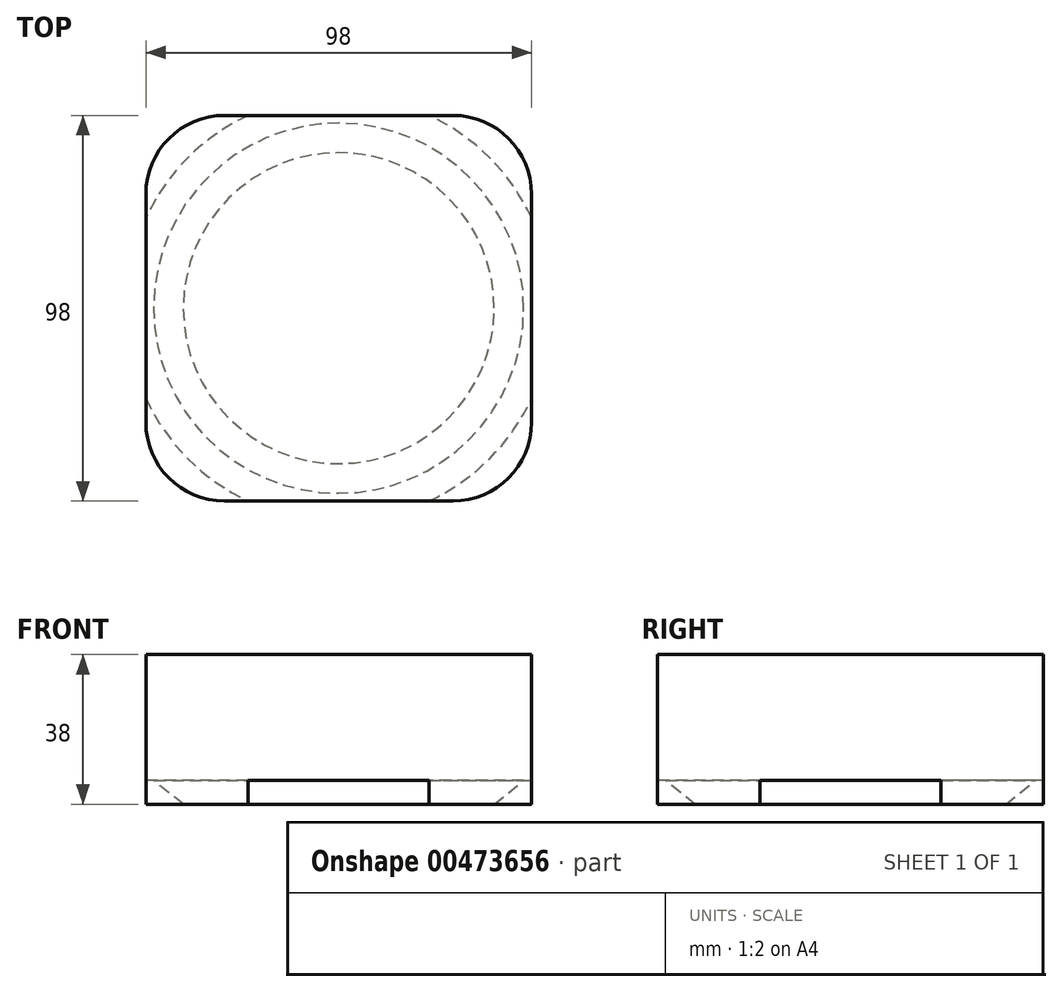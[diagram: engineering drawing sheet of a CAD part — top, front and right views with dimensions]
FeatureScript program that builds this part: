
annotation { "Feature Type Name" : "Feature", "Feature Type Description" : "" }
export const myFeature = defineFeature(function(context is Context, id is Id, definition is map)
    precondition{}
    {
        {
            var Q0;
            Q0=qCreatedBy(makeId("Top.planeOp"),FACE);
            var sketch = newSketch(context, id + "F0", { "sketchPlane" : qUnion([Q0])});
            skLineSegment(sketch, "E0", {"start": v(0, 83.5) * mm, "end": v(0, -80.66) * mm, "construction": true});
            skLineSegment(sketch, "E1", {"start": v(-77.23, 0) * mm, "end": v(78.04, 0) * mm, "construction": true});
            skLineSegment(sketch, "E2.bottom", {"start": v(-49, 49) * mm, "end": v(49, 49) * mm});
            skLineSegment(sketch, "E2.top", {"start": v(-49, -49) * mm, "end": v(49, -49) * mm});
            skLineSegment(sketch, "E2.left", {"start": v(-49, 49) * mm, "end": v(-49, -49) * mm});
            skLineSegment(sketch, "E2.right", {"start": v(49, 49) * mm, "end": v(49, -49) * mm});
            skLineSegment(sketch, "E3", {"start": v(-49, 49) * mm, "end": v(49, -49) * mm, "construction": true});
            skLineSegment(sketch, "E4", {"start": v(49, 49) * mm, "end": v(-49, -49) * mm, "construction": true});
            skPoint(sketch, "E5.positionSnap0", {"position": v(0, 0) * mm});
            skSolve(sketch);
        }
        {
            var Q0;
            Q0 = qSketchRegion(id + "F0", true);
            extrude(context, id + "F1", {"entities" : qUnion([Q0]), "depth" : 38 * mm});
        }
        {
            var Q0;
            Q0=makeQuery(id+"F1.opExtrude","SWEPT_EDGE",EDGE,{"disambiguationData":[OSD([sQuery(id+"F0.wireOp",EDGE,"E2.bottom"),sQuery(id+"F0.wireOp",EDGE,"E2.left")])]});
            var Q1;
            Q1=makeQuery(id+"F1.opExtrude","SWEPT_EDGE",EDGE,{"disambiguationData":[OSD([sQuery(id+"F0.wireOp",EDGE,"E2.bottom"),sQuery(id+"F0.wireOp",EDGE,"E2.right")])]});
            var Q2;
            Q2=makeQuery(id+"F1.opExtrude","SWEPT_EDGE",EDGE,{"disambiguationData":[OSD([sQuery(id+"F0.wireOp",EDGE,"E2.top"),sQuery(id+"F0.wireOp",EDGE,"E2.right")])]});
            var Q3;
            Q3=makeQuery(id+"F1.opExtrude","SWEPT_EDGE",EDGE,{"disambiguationData":[OSD([sQuery(id+"F0.wireOp",EDGE,"E2.top"),sQuery(id+"F0.wireOp",EDGE,"E2.left")])]});
            fillet(context, id + "F2", {"entities" : qUnion([Q0, Q1, Q2, Q3]), "radius" : 20 * mm, "tangentPropagation" : true, "allowEdgeOverflow" : false});
        }
        {
            var Q0;
            Q0=qCreatedBy(makeId("Front.planeOp"),FACE);
            var sketch = newSketch(context, id + "F3", { "sketchPlane" : qUnion([Q0])});
            skLineSegment(sketch, "E6", {"start": v(0, 64.12) * mm, "end": v(0, -29.04) * mm, "construction": true});
            skLineSegment(sketch, "E7", {"start": v(39.5, 0) * mm, "end": v(47, 6) * mm});
            skLineSegment(sketch, "E8", {"start": v(54.12, 0) * mm, "end": v(39.5, 0) * mm});
            skLineSegment(sketch, "E9", {"start": v(47, 6) * mm, "end": v(54.12, 6) * mm});
            skLineSegment(sketch, "E10", {"start": v(54.12, 6) * mm, "end": v(54.12, 0) * mm});
            skSolve(sketch);
        }
        {
            var Q0;
            Q0=makeQuery(id+"F3.imprint","IMPRINT",FACE,{"disambiguationData":[TD([[makeQuery(id+"F3.imprint","IMPRINT",EDGE,{"derivedFrom":sQuery(id+"F3.wireOp",EDGE,"E7")}),-1.0]])]});
            var Q1;
            Q1=sQuery(id+"F3.wireOp",EDGE,"E6");
            revolve(context, id + "F4", {"operationType" : NewBodyOperationType.REMOVE, "entities" : qUnion([Q0]), "axis" : qUnion([Q1]), "revolveType" : RevolveType.FULL, "oppositeDirection" : true});
        }
    });
